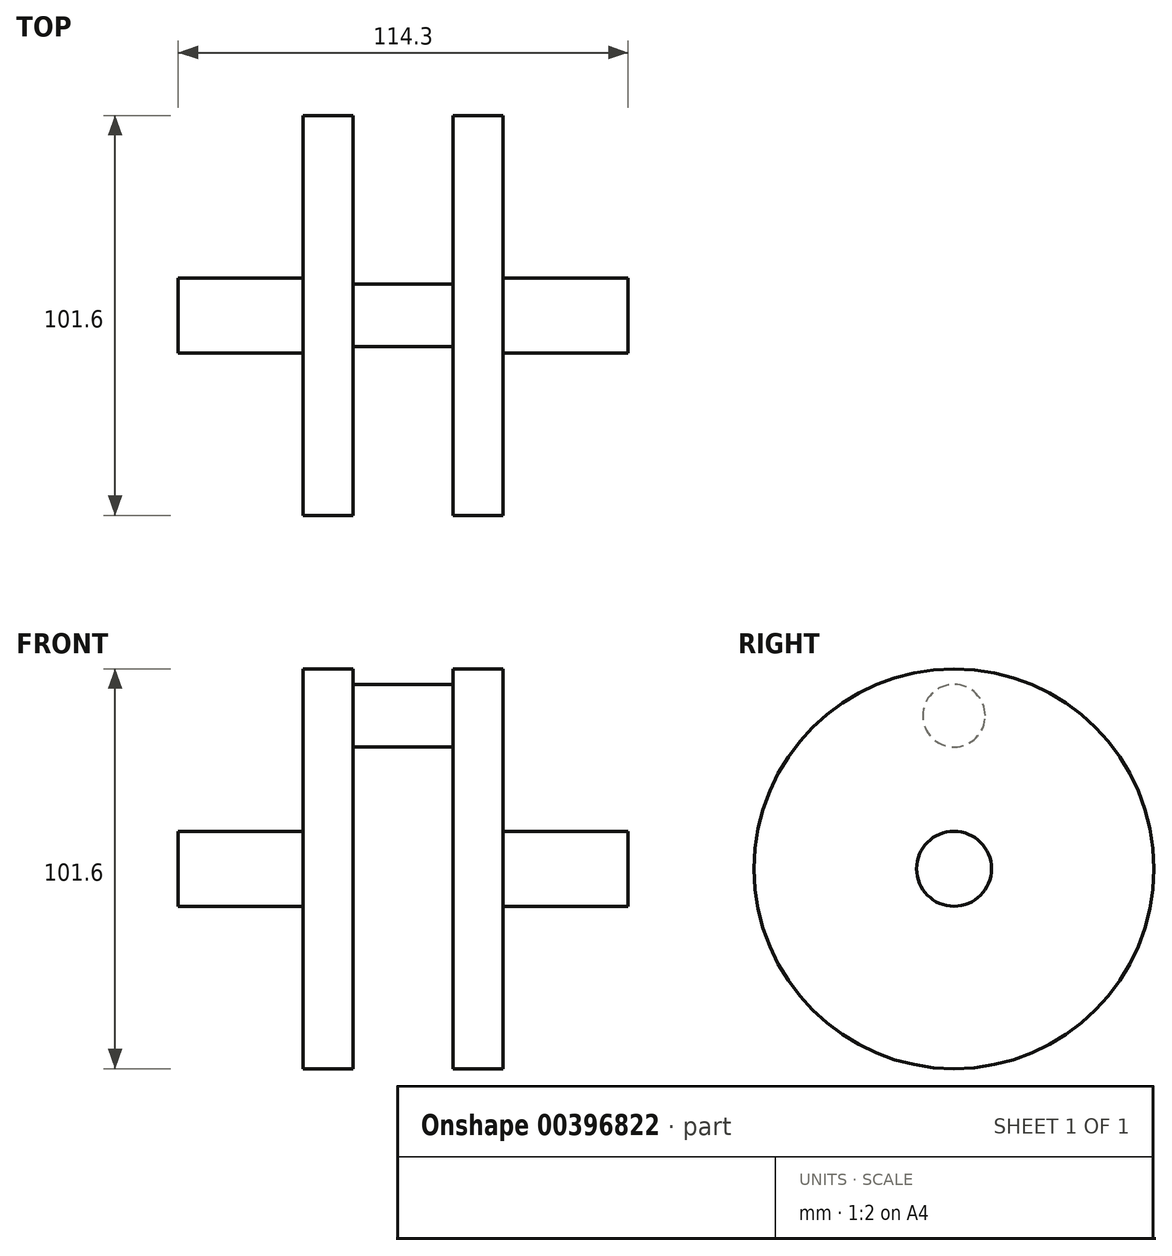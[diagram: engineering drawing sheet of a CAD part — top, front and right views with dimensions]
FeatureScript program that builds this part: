
annotation { "Feature Type Name" : "Feature", "Feature Type Description" : "" }
export const myFeature = defineFeature(function(context is Context, id is Id, definition is map)
    precondition{}
    {
        {
            var Q0;
            Q0=qCreatedBy(makeId("Front.planeOp"),FACE);
            var sketch = newSketch(context, id + "F0", { "sketchPlane" : qUnion([Q0])});
            skLineSegment(sketch, "E0.bottom", {"start": v(-25.4, 0) * mm, "end": v(-57.15, 0) * mm});
            skLineSegment(sketch, "E0.top", {"start": v(-25.4, 9.53) * mm, "end": v(-57.15, 9.53) * mm});
            skLineSegment(sketch, "E0.left", {"start": v(-25.4, 0) * mm, "end": v(-25.4, 9.53) * mm});
            skLineSegment(sketch, "E0.right", {"start": v(-57.15, 0) * mm, "end": v(-57.15, 9.53) * mm});
            skPoint(sketch, "E0.middle", {"position": v(-41.28, 4.76) * mm});
            skLineSegment(sketch, "E1.bottom", {"start": v(-25.4, 0) * mm, "end": v(-12.7, 0) * mm});
            skLineSegment(sketch, "E1.top", {"start": v(-25.4, 50.8) * mm, "end": v(-12.7, 50.8) * mm});
            skLineSegment(sketch, "E1.left", {"start": v(-25.4, 0) * mm, "end": v(-25.4, 50.8) * mm});
            skLineSegment(sketch, "E1.right", {"start": v(-12.7, 0) * mm, "end": v(-12.7, 50.8) * mm});
            skPoint(sketch, "E1.middle", {"position": v(-19.05, 25.4) * mm});
            skLineSegment(sketch, "E2.bottom", {"start": v(57.15, 0) * mm, "end": v(25.4, 0) * mm});
            skLineSegment(sketch, "E2.top", {"start": v(57.15, 9.52) * mm, "end": v(25.4, 9.52) * mm});
            skLineSegment(sketch, "E2.left", {"start": v(57.15, 0) * mm, "end": v(57.15, 9.53) * mm});
            skLineSegment(sketch, "E2.right", {"start": v(25.4, 0) * mm, "end": v(25.4, 9.52) * mm});
            skPoint(sketch, "E2.middle", {"position": v(41.28, 4.76) * mm});
            skLineSegment(sketch, "E3.bottom", {"start": v(25.4, 0) * mm, "end": v(12.7, 0) * mm});
            skLineSegment(sketch, "E3.top", {"start": v(25.4, 50.8) * mm, "end": v(12.7, 50.8) * mm});
            skLineSegment(sketch, "E3.left", {"start": v(25.4, 0) * mm, "end": v(25.4, 50.8) * mm});
            skLineSegment(sketch, "E3.right", {"start": v(12.7, 0) * mm, "end": v(12.7, 50.8) * mm});
            skPoint(sketch, "E3.middle", {"position": v(19.05, 25.4) * mm});
            skLineSegment(sketch, "E4.bottom", {"start": v(-12.7, 46.83) * mm, "end": v(12.7, 46.83) * mm});
            skLineSegment(sketch, "E4.top", {"start": v(-12.7, 38.9) * mm, "end": v(12.7, 38.9) * mm});
            skLineSegment(sketch, "E4.left", {"start": v(-12.7, 46.83) * mm, "end": v(-12.7, 38.9) * mm});
            skLineSegment(sketch, "E4.right", {"start": v(12.7, 46.83) * mm, "end": v(12.7, 38.9) * mm});
            skPoint(sketch, "E4.middle", {"position": v(0, 42.86) * mm});
            skSolve(sketch);
        }
        {
            var Q0;
            {var subQ0=sQuery(id+"F0.wireOp",EDGE,"E0.bottom");Q0=makeQuery(id+"F0.imprint","IMPRINT",FACE,{"disambiguationData":[TD([[makeQuery(id+"F0.imprint","IMPRINT",EDGE,{"derivedFrom":subQ0}),-1.0]])]});}
            var Q1;
            {var subQ3=sQuery(id+"F0.wireOp",EDGE,"E1.bottom");Q1=makeQuery(id+"F0.imprint","IMPRINT",FACE,{"disambiguationData":[TD([[makeQuery(id+"F0.imprint","IMPRINT",EDGE,{"derivedFrom":subQ3}),1.0]])]});}
            var Q2;
            {var subQ3=sQuery(id+"F0.wireOp",EDGE,"E3.bottom");Q2=makeQuery(id+"F0.imprint","IMPRINT",FACE,{"disambiguationData":[TD([[makeQuery(id+"F0.imprint","IMPRINT",EDGE,{"derivedFrom":subQ3}),-1.0]])]});}
            var Q3;
            {var subQ0=sQuery(id+"F0.wireOp",EDGE,"E2.bottom");Q3=makeQuery(id+"F0.imprint","IMPRINT",FACE,{"disambiguationData":[TD([[makeQuery(id+"F0.imprint","IMPRINT",EDGE,{"derivedFrom":subQ0}),-1.0]])]});}
            var Q4;
            Q4=sQuery(id+"F0.wireOp",EDGE,"E0.bottom");
            revolve(context, id + "F1", {"entities" : qUnion([Q0, Q1, Q2, Q3]), "axis" : qUnion([Q4]), "revolveType" : RevolveType.FULL});
        }
        {
            var Q0;
            Q0=qCreatedBy(makeId("Front.planeOp"),FACE);
            var sketch = newSketch(context, id + "F2", { "sketchPlane" : qUnion([Q0])});
            skLineSegment(sketch, "E5.bottom", {"start": v(-12.7, 38.9) * mm, "end": v(12.7, 38.9) * mm});
            skLineSegment(sketch, "E5.top", {"start": v(-12.7, 46.83) * mm, "end": v(12.7, 46.83) * mm});
            skLineSegment(sketch, "E5.left", {"start": v(-12.7, 38.9) * mm, "end": v(-12.7, 46.83) * mm});
            skLineSegment(sketch, "E5.right", {"start": v(12.7, 38.9) * mm, "end": v(12.7, 46.83) * mm});
            skPoint(sketch, "E5.middle", {"position": v(0, 42.86) * mm});
            skSolve(sketch);
        }
        {
            var Q0;
            Q0=makeQuery(id+"F2.imprint","IMPRINT",FACE,{"disambiguationData":[TD([[makeQuery(id+"F2.imprint","IMPRINT",EDGE,{"derivedFrom":sQuery(id+"F2.wireOp",EDGE,"E5.bottom")}),1.0]])]});
            var Q1;
            Q1=sQuery(id+"F2.wireOp",EDGE,"E5.bottom");
            revolve(context, id + "F3", {"entities" : qUnion([Q0]), "axis" : qUnion([Q1]), "revolveType" : RevolveType.FULL});
        }
    });
